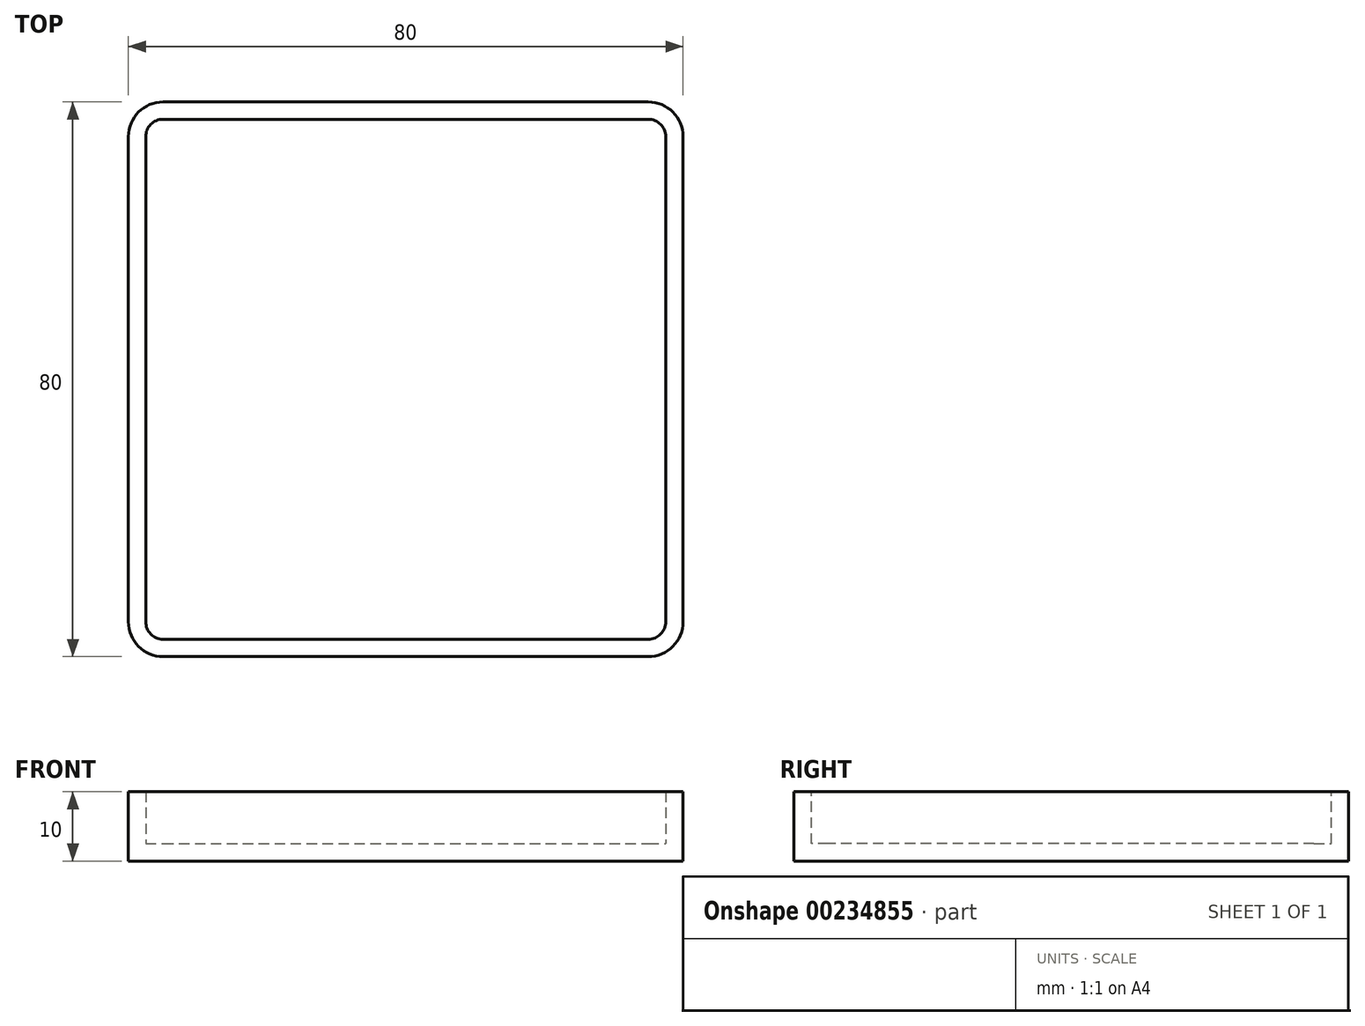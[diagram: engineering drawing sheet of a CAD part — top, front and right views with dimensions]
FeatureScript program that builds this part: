
annotation { "Feature Type Name" : "Feature", "Feature Type Description" : "" }
export const myFeature = defineFeature(function(context is Context, id is Id, definition is map)
    precondition{}
    {
        {
            var Q0;
            Q0=qCreatedBy(makeId("Top.planeOp"),FACE);
            var sketch = newSketch(context, id + "F0", { "sketchPlane" : qUnion([Q0])});
            skLineSegment(sketch, "E0.bottom", {"start": v(-40, 40) * mm, "end": v(40, 40) * mm});
            skLineSegment(sketch, "E0.top", {"start": v(-40, -40) * mm, "end": v(40, -40) * mm});
            skLineSegment(sketch, "E0.left", {"start": v(-40, 40) * mm, "end": v(-40, -40) * mm});
            skLineSegment(sketch, "E0.right", {"start": v(40, 40) * mm, "end": v(40, -40) * mm});
            skPoint(sketch, "E0.middle", {"position": v(0, 0) * mm});
            skSolve(sketch);
        }
        {
            var Q0;
            Q0 = qSketchRegion(id + "F0", true);
            extrude(context, id + "F3", {"entities" : qUnion([Q0]), "depth" : 10 * mm});
        }
        {
            var Q0;
            Q0=makeQuery(id+"F3.opExtrude","SWEPT_EDGE",EDGE,{"disambiguationData":[OSD([sQuery(id+"F0.wireOp",EDGE,"E0.top"),sQuery(id+"F0.wireOp",EDGE,"E0.left")])]});
            var Q1;
            Q1=makeQuery(id+"F3.opExtrude","SWEPT_EDGE",EDGE,{"disambiguationData":[OSD([sQuery(id+"F0.wireOp",EDGE,"E0.top"),sQuery(id+"F0.wireOp",EDGE,"E0.right")])]});
            var Q2;
            Q2=makeQuery(id+"F3.opExtrude","SWEPT_EDGE",EDGE,{"disambiguationData":[OSD([sQuery(id+"F0.wireOp",EDGE,"E0.bottom"),sQuery(id+"F0.wireOp",EDGE,"E0.right")])]});
            var Q3;
            Q3=makeQuery(id+"F3.opExtrude","SWEPT_EDGE",EDGE,{"disambiguationData":[OSD([sQuery(id+"F0.wireOp",EDGE,"E0.bottom"),sQuery(id+"F0.wireOp",EDGE,"E0.left")])]});
            fillet(context, id + "F1", {"entities" : qUnion([Q0, Q1, Q2, Q3]), "radius" : 5 * mm, "tangentPropagation" : true, "allowEdgeOverflow" : false});
        }
        {
            var Q0;
            Q0=makeQuery(id+"F3.opExtrude","CAP_FACE",FACE,{"disambiguationData":[OSD([sQuery(id+"F0.wireOp",EDGE,"E0.bottom"),sQuery(id+"F0.wireOp",EDGE,"E0.top"),sQuery(id+"F0.wireOp",EDGE,"E0.left"),sQuery(id+"F0.wireOp",EDGE,"E0.right")])],"isStart":false});
            shell(context, id + "F2", {"entities" : qUnion([Q0]), "thickness" : 2.5 * mm});
        }
    });
